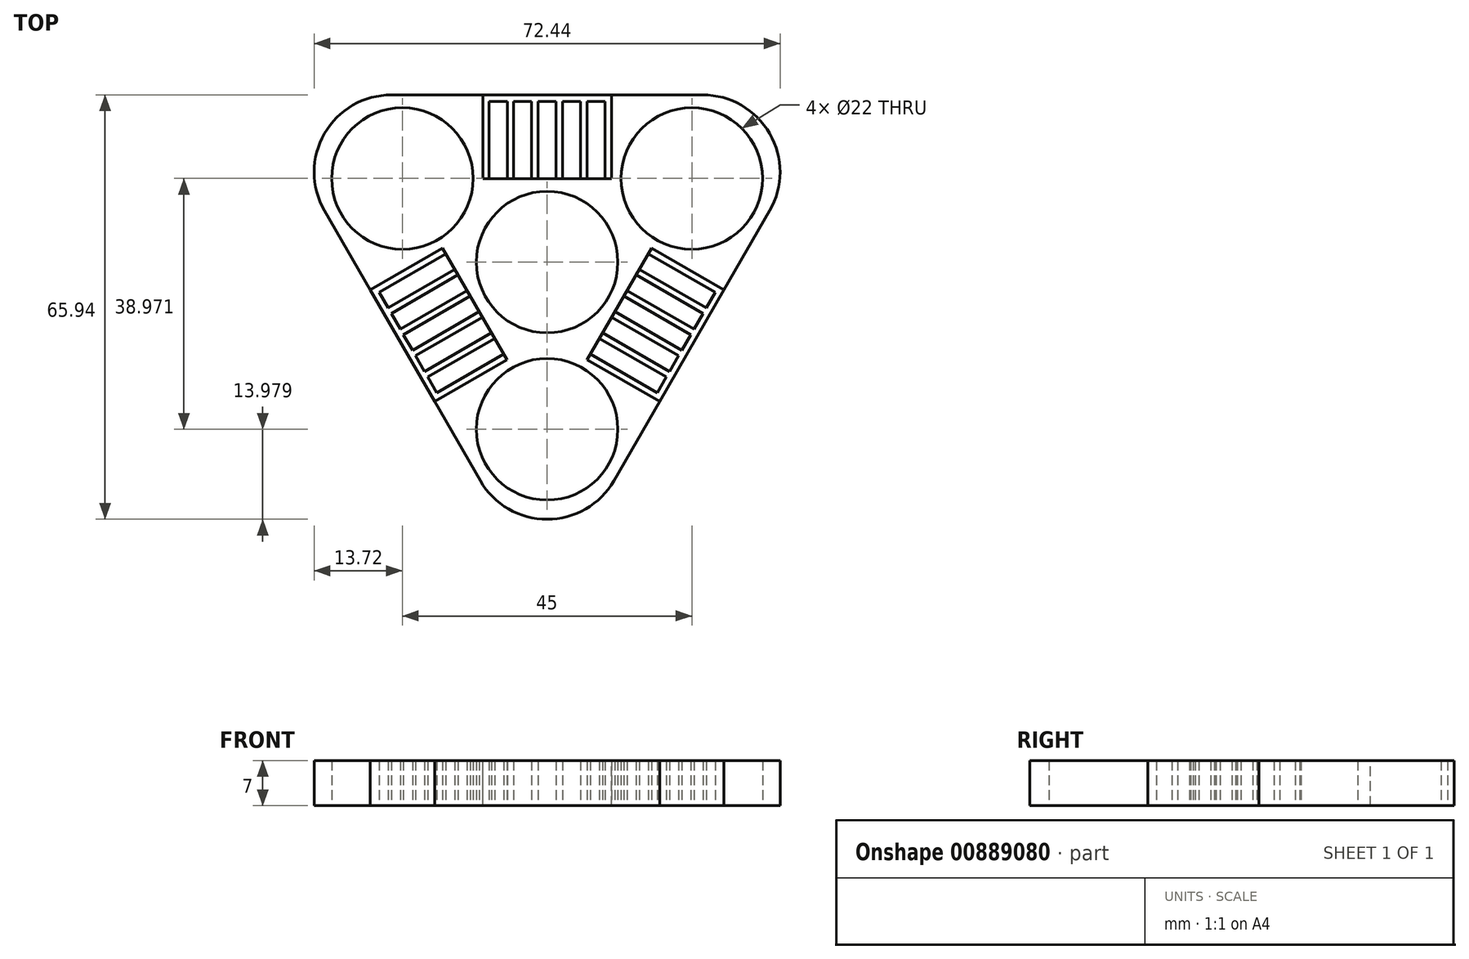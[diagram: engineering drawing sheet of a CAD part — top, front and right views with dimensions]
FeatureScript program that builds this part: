
annotation { "Feature Type Name" : "Feature", "Feature Type Description" : "" }
export const myFeature = defineFeature(function(context is Context, id is Id, definition is map)
    precondition{}
    {
        {
            var Q0;
            Q0=qCreatedBy(makeId("Top.planeOp"),FACE);
            var sketch = newSketch(context, id + "F0", { "sketchPlane" : qUnion([Q0])});
            skCircle(sketch, "E0.cCircle", {"center": v(0, 0) * mm, "radius": 25.98 * mm, "construction": true});
            skLineSegment(sketch, "E0.0", {"start": v(-45, 25.98) * mm, "end": v(45, 25.98) * mm});
            skLineSegment(sketch, "E0.1", {"start": v(45, 25.98) * mm, "end": v(0, -51.96) * mm});
            skLineSegment(sketch, "E0.2", {"start": v(0, -51.96) * mm, "end": v(-45, 25.98) * mm});
            skPoint(sketch, "E0.0.midPoint", {"position": v(0, 25.98) * mm});
            skCircle(sketch, "E1", {"center": v(0, 0) * mm, "radius": 11 * mm});
            skLineSegment(sketch, "E2", {"start": v(0, 0) * mm, "end": v(0, -51.96) * mm, "construction": true});
            skLineSegment(sketch, "E3", {"start": v(0, 0) * mm, "end": v(-45, 25.98) * mm, "construction": true});
            skLineSegment(sketch, "E4", {"start": v(0, 0) * mm, "end": v(45, 25.98) * mm, "construction": true});
            skCircle(sketch, "E5", {"center": v(-22.5, 13) * mm, "radius": 11 * mm});
            skCircle(sketch, "E6", {"center": v(0, -25.98) * mm, "radius": 11 * mm});
            skCircle(sketch, "E7", {"center": v(22.5, 13) * mm, "radius": 11 * mm});
            skSolve(sketch);
        }
        {
            var Q0;
            Q0=makeQuery(id+"F0.imprint","IMPRINT",FACE,{"disambiguationData":[TD([[makeQuery(id+"F0.imprint","IMPRINT",EDGE,{"derivedFrom":sQuery(id+"F0.wireOp",EDGE,"E0.0")}),-1.0]])]});
            extrude(context, id + "F1", {"entities" : qUnion([Q0]), "depth" : 7 * mm, "offsetDistance" : 25 * mm});
        }
        {
            var Q0;
            Q0=makeQuery(id+"F1.opExtrude","SWEPT_EDGE",EDGE,{"disambiguationData":[OSD([sQuery(id+"F0.wireOp",EDGE,"E0.0"),sQuery(id+"F0.wireOp",EDGE,"E0.2")])]});
            var Q1;
            Q1=makeQuery(id+"F1.opExtrude","SWEPT_EDGE",EDGE,{"disambiguationData":[OSD([sQuery(id+"F0.wireOp",EDGE,"E0.1"),sQuery(id+"F0.wireOp",EDGE,"E0.2")])]});
            var Q2;
            Q2=makeQuery(id+"F1.opExtrude","SWEPT_EDGE",EDGE,{"disambiguationData":[OSD([sQuery(id+"F0.wireOp",EDGE,"E0.0"),sQuery(id+"F0.wireOp",EDGE,"E0.1")])]});
            fillet(context, id + "F2", {"entities" : qUnion([Q0, Q1, Q2]), "radius" : 12 * mm, "tangentPropagation" : true, "allowEdgeOverflow" : false});
        }
        {
            var Q0;
            Q0=makeQuery(id+"F1.opExtrude","CAP_FACE",FACE,{"disambiguationData":[OSD([sQuery(id+"F0.wireOp",EDGE,"E0.0"),sQuery(id+"F0.wireOp",EDGE,"E0.1"),sQuery(id+"F0.wireOp",EDGE,"E0.2"),sQuery(id+"F0.wireOp",EDGE,"E1"),sQuery(id+"F0.wireOp",EDGE,"E5"),sQuery(id+"F0.wireOp",EDGE,"E6"),sQuery(id+"F0.wireOp",EDGE,"E7")])],"isStart":false});
            var sketch = newSketch(context, id + "F3", { "sketchPlane" : qUnion([Q0])});
            skCircle(sketch, "E8", {"center": v(0, 0) * mm, "radius": 40 * mm});
            skLineSegment(sketch, "E9.bottom", {"start": v(10, 12.98) * mm, "end": v(-10, 12.98) * mm});
            skLineSegment(sketch, "E9.top", {"start": v(10, 38.98) * mm, "end": v(-10, 38.98) * mm});
            skLineSegment(sketch, "E9.left", {"start": v(10, 12.98) * mm, "end": v(10, 38.98) * mm});
            skLineSegment(sketch, "E9.right", {"start": v(-10, 12.98) * mm, "end": v(-10, 38.98) * mm});
            skPoint(sketch, "E9.middle", {"position": v(0, 25.98) * mm});
            skLineSegment(sketch, "E10.1.0", {"start": v(-6.24, -15.15) * mm, "end": v(-28.76, -28.15) * mm});
            skLineSegment(sketch, "E10.1.1", {"start": v(-16.24, 2.17) * mm, "end": v(-6.24, -15.15) * mm});
            skLineSegment(sketch, "E10.1.2", {"start": v(-16.24, 2.17) * mm, "end": v(-38.76, -10.83) * mm});
            skLineSegment(sketch, "E10.1.3", {"start": v(-38.76, -10.83) * mm, "end": v(-28.76, -28.15) * mm});
            skLineSegment(sketch, "E10.2.0", {"start": v(16.24, 2.17) * mm, "end": v(38.76, -10.83) * mm});
            skLineSegment(sketch, "E10.2.1", {"start": v(6.24, -15.15) * mm, "end": v(16.24, 2.17) * mm});
            skLineSegment(sketch, "E10.2.2", {"start": v(6.24, -15.15) * mm, "end": v(28.76, -28.15) * mm});
            skLineSegment(sketch, "E10.2.3", {"start": v(28.76, -28.15) * mm, "end": v(38.76, -10.83) * mm});
            skSolve(sketch);
        }
        {
            var Q0;
            {var subQ0=sQuery(id+"F3.wireOp",EDGE,"E9.bottom");Q0=makeQuery(id+"F3.imprint","IMPRINT",FACE,{"disambiguationData":[TD([[makeQuery(id+"F3.imprint","IMPRINT",EDGE,{"derivedFrom":subQ0}),-1.0]])]});}
            var Q1;
            {var subQ0=sQuery(id+"F3.wireOp",EDGE,"E10.2.1");Q1=makeQuery(id+"F3.imprint","IMPRINT",FACE,{"disambiguationData":[TD([[makeQuery(id+"F3.imprint","IMPRINT",EDGE,{"derivedFrom":subQ0}),-1.0]])]});}
            var Q2;
            {var subQ0=sQuery(id+"F3.wireOp",EDGE,"E10.1.1");Q2=makeQuery(id+"F3.imprint","IMPRINT",FACE,{"disambiguationData":[TD([[makeQuery(id+"F3.imprint","IMPRINT",EDGE,{"derivedFrom":subQ0}),-1.0]])]});}
            extrude(context, id + "F4", {"entities" : qUnion([Q0, Q1, Q2]), "operationType" : NewBodyOperationType.REMOVE, "oppositeDirection" : true, "depth" : 25 * mm, "offsetDistance" : 25 * mm});
        }
        {
            var Q0;
            Q0=qCreatedBy(makeId("Top.planeOp"),FACE);
            var sketch = newSketch(context, id + "F5", { "sketchPlane" : qUnion([Q0])});
            skLineSegment(sketch, "E11.0", {"start": v(-24.22, 25.98) * mm, "end": v(-10, 25.98) * mm, "construction": true});
            skLineSegment(sketch, "E12.0", {"start": v(-10, 12.98) * mm, "end": v(-10, 25.98) * mm, "construction": true});
            skLineSegment(sketch, "E13.0", {"start": v(10, 12.98) * mm, "end": v(-10, 12.98) * mm});
            skLineSegment(sketch, "E14.0", {"start": v(10, 12.98) * mm, "end": v(10, 25.98) * mm, "construction": true});
            skLineSegment(sketch, "E15.0", {"start": v(10, 25.98) * mm, "end": v(24.22, 25.98) * mm, "construction": true});
            skLineSegment(sketch, "E16.bottom", {"start": v(-10, 25.98) * mm, "end": v(-9, 25.98) * mm});
            skLineSegment(sketch, "E16.top", {"start": v(-10, 12.98) * mm, "end": v(-9, 12.98) * mm});
            skLineSegment(sketch, "E16.left", {"start": v(-10, 25.98) * mm, "end": v(-10, 12.98) * mm});
            skLineSegment(sketch, "E16.right", {"start": v(-9, 25.98) * mm, "end": v(-9, 12.98) * mm});
            skLineSegment(sketch, "E17.1.0.0", {"start": v(-8.1, 25.98) * mm, "end": v(-8.1, 12.98) * mm});
            skLineSegment(sketch, "E17.1.0.1", {"start": v(-8.1, 25.98) * mm, "end": v(-7.1, 25.98) * mm});
            skLineSegment(sketch, "E17.1.0.2", {"start": v(-7.1, 25.98) * mm, "end": v(-7.1, 12.98) * mm});
            skLineSegment(sketch, "E17.2.0.0", {"start": v(-6.2, 25.98) * mm, "end": v(-6.2, 12.98) * mm});
            skLineSegment(sketch, "E17.2.0.1", {"start": v(-6.2, 25.98) * mm, "end": v(-5.2, 25.98) * mm});
            skLineSegment(sketch, "E17.2.0.2", {"start": v(-5.2, 25.98) * mm, "end": v(-5.2, 12.98) * mm});
            skLineSegment(sketch, "E17.3.0.0", {"start": v(-4.3, 25.98) * mm, "end": v(-4.3, 12.98) * mm});
            skLineSegment(sketch, "E17.3.0.1", {"start": v(-4.3, 25.98) * mm, "end": v(-3.3, 25.98) * mm});
            skLineSegment(sketch, "E17.3.0.2", {"start": v(-3.3, 25.98) * mm, "end": v(-3.3, 12.98) * mm});
            skLineSegment(sketch, "E17.4.0.0", {"start": v(-2.4, 25.98) * mm, "end": v(-2.4, 12.98) * mm});
            skLineSegment(sketch, "E17.4.0.1", {"start": v(-2.4, 25.98) * mm, "end": v(-1.4, 25.98) * mm});
            skLineSegment(sketch, "E17.4.0.2", {"start": v(-1.4, 25.98) * mm, "end": v(-1.4, 12.98) * mm});
            skLineSegment(sketch, "E17.5.0.0", {"start": v(-0.5, 25.98) * mm, "end": v(-0.5, 12.98) * mm});
            skLineSegment(sketch, "E17.5.0.1", {"start": v(-0.5, 25.98) * mm, "end": v(0.5, 25.98) * mm});
            skLineSegment(sketch, "E17.5.0.2", {"start": v(0.5, 25.98) * mm, "end": v(0.5, 12.98) * mm});
            skLineSegment(sketch, "E17.6.0.0", {"start": v(1.4, 25.98) * mm, "end": v(1.4, 12.98) * mm});
            skLineSegment(sketch, "E17.6.0.1", {"start": v(1.4, 25.98) * mm, "end": v(2.4, 25.98) * mm});
            skLineSegment(sketch, "E17.6.0.2", {"start": v(2.4, 25.98) * mm, "end": v(2.4, 12.98) * mm});
            skLineSegment(sketch, "E17.7.0.0", {"start": v(3.3, 25.98) * mm, "end": v(3.3, 12.98) * mm});
            skLineSegment(sketch, "E17.7.0.1", {"start": v(3.3, 25.98) * mm, "end": v(4.3, 25.98) * mm});
            skLineSegment(sketch, "E17.7.0.2", {"start": v(4.3, 25.98) * mm, "end": v(4.3, 12.98) * mm});
            skLineSegment(sketch, "E17.8.0.0", {"start": v(5.2, 25.98) * mm, "end": v(5.2, 12.98) * mm});
            skLineSegment(sketch, "E17.8.0.1", {"start": v(5.2, 25.98) * mm, "end": v(6.2, 25.98) * mm});
            skLineSegment(sketch, "E17.8.0.2", {"start": v(6.2, 25.98) * mm, "end": v(6.2, 12.98) * mm});
            skLineSegment(sketch, "E17.9.0.0", {"start": v(7.1, 25.98) * mm, "end": v(7.1, 12.98) * mm});
            skLineSegment(sketch, "E17.9.0.1", {"start": v(7.1, 25.98) * mm, "end": v(8.1, 25.98) * mm});
            skLineSegment(sketch, "E17.9.0.2", {"start": v(8.1, 25.98) * mm, "end": v(8.1, 12.98) * mm});
            skLineSegment(sketch, "E17.direction1", {"start": v(-10, 12.98) * mm, "end": v(-8.1, 12.98) * mm, "construction": true});
            skLineSegment(sketch, "E18.bottom", {"start": v(-10, 25.98) * mm, "end": v(10, 25.98) * mm});
            skLineSegment(sketch, "E18.top", {"start": v(-10, 24.98) * mm, "end": v(10, 24.98) * mm});
            skLineSegment(sketch, "E18.left", {"start": v(-10, 25.98) * mm, "end": v(-10, 24.98) * mm});
            skLineSegment(sketch, "E18.right", {"start": v(10, 25.98) * mm, "end": v(10, 24.98) * mm});
            skLineSegment(sketch, "E19.0.10.0", {"start": v(9, 25.98) * mm, "end": v(9, 12.98) * mm});
            skLineSegment(sketch, "E19.3.10.0", {"start": v(9, 25.98) * mm, "end": v(10, 25.98) * mm});
            skLineSegment(sketch, "E19.6.10.0", {"start": v(10, 25.98) * mm, "end": v(10, 12.98) * mm});
            skSolve(sketch);
        }
        {
            var Q0;
            {var subQ0=sQuery(id+"F5.wireOp",EDGE,"E16.left");var subQ1=sQuery(id+"F5.wireOp",EDGE,"E13.0");var subQ2=makeQuery(id+"F5.imprint","INTERSECT",VERTEX,{"derivedFrom":[subQ1,subQ0]});Q0=makeQuery(id+"F5.imprint","IMPRINT",FACE,{"disambiguationData":[TD([[makeQuery(id+"F5.imprint","IMPRINT",EDGE,{"disambiguationData":[TD([[subQ2,1.0]])],"derivedFrom":subQ1}),-1.0]])]});}
            var Q1;
            {var subQ0=sQuery(id+"F5.wireOp",EDGE,"E17.2.0.2");var subQ1=sQuery(id+"F5.wireOp",EDGE,"E13.0");var subQ2=makeQuery(id+"F5.imprint","INTERSECT",VERTEX,{"derivedFrom":[subQ1,subQ0]});Q1=makeQuery(id+"F5.imprint","IMPRINT",FACE,{"disambiguationData":[TD([[makeQuery(id+"F5.imprint","IMPRINT",EDGE,{"disambiguationData":[TD([[subQ2,-1.0]])],"derivedFrom":subQ1}),-1.0]])]});}
            var Q2;
            {var subQ0=sQuery(id+"F5.wireOp",EDGE,"E17.4.0.0");var subQ1=sQuery(id+"F5.wireOp",EDGE,"E13.0");var subQ2=makeQuery(id+"F5.imprint","INTERSECT",VERTEX,{"derivedFrom":[subQ1,subQ0]});Q2=makeQuery(id+"F5.imprint","IMPRINT",FACE,{"disambiguationData":[TD([[makeQuery(id+"F5.imprint","IMPRINT",EDGE,{"disambiguationData":[TD([[subQ2,1.0]])],"derivedFrom":subQ1}),-1.0]])]});}
            var Q3;
            {var subQ0=sQuery(id+"F5.wireOp",EDGE,"E17.6.0.0");var subQ1=sQuery(id+"F5.wireOp",EDGE,"E13.0");var subQ2=makeQuery(id+"F5.imprint","INTERSECT",VERTEX,{"derivedFrom":[subQ1,subQ0]});Q3=makeQuery(id+"F5.imprint","IMPRINT",FACE,{"disambiguationData":[TD([[makeQuery(id+"F5.imprint","IMPRINT",EDGE,{"disambiguationData":[TD([[subQ2,1.0]])],"derivedFrom":subQ1}),-1.0]])]});}
            var Q4;
            {var subQ0=sQuery(id+"F5.wireOp",EDGE,"E17.8.0.2");var subQ1=sQuery(id+"F5.wireOp",EDGE,"E13.0");var subQ2=makeQuery(id+"F5.imprint","INTERSECT",VERTEX,{"derivedFrom":[subQ1,subQ0]});Q4=makeQuery(id+"F5.imprint","IMPRINT",FACE,{"disambiguationData":[TD([[makeQuery(id+"F5.imprint","IMPRINT",EDGE,{"disambiguationData":[TD([[subQ2,-1.0]])],"derivedFrom":subQ1}),-1.0]])]});}
            var Q5;
            {var subQ0=sQuery(id+"F5.wireOp",EDGE,"E19.6.10.0");Q5=makeQuery(id+"F5.imprint","IMPRINT",FACE,{"disambiguationData":[TD([[makeQuery(id+"F5.imprint","IMPRINT",EDGE,{"derivedFrom":subQ0}),-1.0]])]});}
            var Q6;
            {var subQ3=sQuery(id+"F5.wireOp",EDGE,"E18.right");Q6=makeQuery(id+"F5.imprint","IMPRINT",FACE,{"disambiguationData":[TD([[makeQuery(id+"F5.imprint","IMPRINT",EDGE,{"derivedFrom":subQ3}),-1.0]])]});}
            var Q7;
            {var subQ1=sQuery(id+"F5.wireOp",EDGE,"E17.9.0.2");var subQ3=sQuery(id+"F5.wireOp",EDGE,"E18.top");var subQ4=makeQuery(id+"F5.imprint","INTERSECT",VERTEX,{"derivedFrom":[subQ1,subQ3]});Q7=makeQuery(id+"F5.imprint","IMPRINT",FACE,{"disambiguationData":[TD([[makeQuery(id+"F5.imprint","IMPRINT",EDGE,{"disambiguationData":[TD([[subQ4,-1.0]])],"derivedFrom":subQ3}),1.0]])]});}
            var Q8;
            {var subQ4=sQuery(id+"F5.wireOp",EDGE,"E17.9.0.1");Q8=makeQuery(id+"F5.imprint","IMPRINT",FACE,{"disambiguationData":[TD([[makeQuery(id+"F5.imprint","IMPRINT",EDGE,{"derivedFrom":subQ4}),-1.0]])]});}
            var Q9;
            {var subQ1=sQuery(id+"F5.wireOp",EDGE,"E17.8.0.2");var subQ3=sQuery(id+"F5.wireOp",EDGE,"E18.top");var subQ4=makeQuery(id+"F5.imprint","INTERSECT",VERTEX,{"derivedFrom":[subQ1,subQ3]});Q9=makeQuery(id+"F5.imprint","IMPRINT",FACE,{"disambiguationData":[TD([[makeQuery(id+"F5.imprint","IMPRINT",EDGE,{"disambiguationData":[TD([[subQ4,-1.0]])],"derivedFrom":subQ3}),1.0]])]});}
            var Q10;
            {var subQ4=sQuery(id+"F5.wireOp",EDGE,"E17.8.0.1");Q10=makeQuery(id+"F5.imprint","IMPRINT",FACE,{"disambiguationData":[TD([[makeQuery(id+"F5.imprint","IMPRINT",EDGE,{"derivedFrom":subQ4}),-1.0]])]});}
            var Q11;
            {var subQ1=sQuery(id+"F5.wireOp",EDGE,"E17.7.0.2");var subQ3=sQuery(id+"F5.wireOp",EDGE,"E18.top");var subQ4=makeQuery(id+"F5.imprint","INTERSECT",VERTEX,{"derivedFrom":[subQ1,subQ3]});Q11=makeQuery(id+"F5.imprint","IMPRINT",FACE,{"disambiguationData":[TD([[makeQuery(id+"F5.imprint","IMPRINT",EDGE,{"disambiguationData":[TD([[subQ4,-1.0]])],"derivedFrom":subQ3}),1.0]])]});}
            var Q12;
            {var subQ4=sQuery(id+"F5.wireOp",EDGE,"E17.7.0.1");Q12=makeQuery(id+"F5.imprint","IMPRINT",FACE,{"disambiguationData":[TD([[makeQuery(id+"F5.imprint","IMPRINT",EDGE,{"derivedFrom":subQ4}),-1.0]])]});}
            var Q13;
            {var subQ1=sQuery(id+"F5.wireOp",EDGE,"E17.6.0.2");var subQ3=sQuery(id+"F5.wireOp",EDGE,"E18.top");var subQ4=makeQuery(id+"F5.imprint","INTERSECT",VERTEX,{"derivedFrom":[subQ1,subQ3]});Q13=makeQuery(id+"F5.imprint","IMPRINT",FACE,{"disambiguationData":[TD([[makeQuery(id+"F5.imprint","IMPRINT",EDGE,{"disambiguationData":[TD([[subQ4,-1.0]])],"derivedFrom":subQ3}),1.0]])]});}
            var Q14;
            {var subQ4=sQuery(id+"F5.wireOp",EDGE,"E17.6.0.1");Q14=makeQuery(id+"F5.imprint","IMPRINT",FACE,{"disambiguationData":[TD([[makeQuery(id+"F5.imprint","IMPRINT",EDGE,{"derivedFrom":subQ4}),-1.0]])]});}
            var Q15;
            {var subQ1=sQuery(id+"F5.wireOp",EDGE,"E17.5.0.2");var subQ3=sQuery(id+"F5.wireOp",EDGE,"E18.top");var subQ4=makeQuery(id+"F5.imprint","INTERSECT",VERTEX,{"derivedFrom":[subQ1,subQ3]});Q15=makeQuery(id+"F5.imprint","IMPRINT",FACE,{"disambiguationData":[TD([[makeQuery(id+"F5.imprint","IMPRINT",EDGE,{"disambiguationData":[TD([[subQ4,-1.0]])],"derivedFrom":subQ3}),1.0]])]});}
            var Q16;
            {var subQ4=sQuery(id+"F5.wireOp",EDGE,"E17.5.0.1");Q16=makeQuery(id+"F5.imprint","IMPRINT",FACE,{"disambiguationData":[TD([[makeQuery(id+"F5.imprint","IMPRINT",EDGE,{"derivedFrom":subQ4}),-1.0]])]});}
            var Q17;
            {var subQ1=sQuery(id+"F5.wireOp",EDGE,"E17.4.0.2");var subQ3=sQuery(id+"F5.wireOp",EDGE,"E18.top");var subQ4=makeQuery(id+"F5.imprint","INTERSECT",VERTEX,{"derivedFrom":[subQ1,subQ3]});Q17=makeQuery(id+"F5.imprint","IMPRINT",FACE,{"disambiguationData":[TD([[makeQuery(id+"F5.imprint","IMPRINT",EDGE,{"disambiguationData":[TD([[subQ4,-1.0]])],"derivedFrom":subQ3}),1.0]])]});}
            var Q18;
            {var subQ4=sQuery(id+"F5.wireOp",EDGE,"E17.4.0.1");Q18=makeQuery(id+"F5.imprint","IMPRINT",FACE,{"disambiguationData":[TD([[makeQuery(id+"F5.imprint","IMPRINT",EDGE,{"derivedFrom":subQ4}),-1.0]])]});}
            var Q19;
            {var subQ1=sQuery(id+"F5.wireOp",EDGE,"E17.3.0.2");var subQ3=sQuery(id+"F5.wireOp",EDGE,"E18.top");var subQ4=makeQuery(id+"F5.imprint","INTERSECT",VERTEX,{"derivedFrom":[subQ1,subQ3]});Q19=makeQuery(id+"F5.imprint","IMPRINT",FACE,{"disambiguationData":[TD([[makeQuery(id+"F5.imprint","IMPRINT",EDGE,{"disambiguationData":[TD([[subQ4,-1.0]])],"derivedFrom":subQ3}),1.0]])]});}
            var Q20;
            {var subQ4=sQuery(id+"F5.wireOp",EDGE,"E17.3.0.1");Q20=makeQuery(id+"F5.imprint","IMPRINT",FACE,{"disambiguationData":[TD([[makeQuery(id+"F5.imprint","IMPRINT",EDGE,{"derivedFrom":subQ4}),-1.0]])]});}
            var Q21;
            {var subQ1=sQuery(id+"F5.wireOp",EDGE,"E17.2.0.2");var subQ3=sQuery(id+"F5.wireOp",EDGE,"E18.top");var subQ4=makeQuery(id+"F5.imprint","INTERSECT",VERTEX,{"derivedFrom":[subQ1,subQ3]});Q21=makeQuery(id+"F5.imprint","IMPRINT",FACE,{"disambiguationData":[TD([[makeQuery(id+"F5.imprint","IMPRINT",EDGE,{"disambiguationData":[TD([[subQ4,-1.0]])],"derivedFrom":subQ3}),1.0]])]});}
            var Q22;
            {var subQ4=sQuery(id+"F5.wireOp",EDGE,"E17.2.0.1");Q22=makeQuery(id+"F5.imprint","IMPRINT",FACE,{"disambiguationData":[TD([[makeQuery(id+"F5.imprint","IMPRINT",EDGE,{"derivedFrom":subQ4}),-1.0]])]});}
            var Q23;
            {var subQ1=sQuery(id+"F5.wireOp",EDGE,"E17.1.0.2");var subQ3=sQuery(id+"F5.wireOp",EDGE,"E18.top");var subQ4=makeQuery(id+"F5.imprint","INTERSECT",VERTEX,{"derivedFrom":[subQ1,subQ3]});Q23=makeQuery(id+"F5.imprint","IMPRINT",FACE,{"disambiguationData":[TD([[makeQuery(id+"F5.imprint","IMPRINT",EDGE,{"disambiguationData":[TD([[subQ4,-1.0]])],"derivedFrom":subQ3}),1.0]])]});}
            var Q24;
            {var subQ4=sQuery(id+"F5.wireOp",EDGE,"E17.1.0.1");Q24=makeQuery(id+"F5.imprint","IMPRINT",FACE,{"disambiguationData":[TD([[makeQuery(id+"F5.imprint","IMPRINT",EDGE,{"derivedFrom":subQ4}),-1.0]])]});}
            var Q25;
            {var subQ1=sQuery(id+"F5.wireOp",EDGE,"E16.right");var subQ3=sQuery(id+"F5.wireOp",EDGE,"E18.top");var subQ4=makeQuery(id+"F5.imprint","INTERSECT",VERTEX,{"derivedFrom":[subQ1,subQ3]});Q25=makeQuery(id+"F5.imprint","IMPRINT",FACE,{"disambiguationData":[TD([[makeQuery(id+"F5.imprint","IMPRINT",EDGE,{"disambiguationData":[TD([[subQ4,-1.0]])],"derivedFrom":subQ3}),1.0]])]});}
            var Q26;
            {var subQ0=sQuery(id+"F5.wireOp",EDGE,"E16.bottom");Q26=makeQuery(id+"F5.imprint","IMPRINT",FACE,{"disambiguationData":[TD([[makeQuery(id+"F5.imprint","IMPRINT",EDGE,{"derivedFrom":subQ0}),-1.0]])]});}
            extrude(context, id + "F6", {"entities" : qUnion([Q0, Q1, Q2, Q3, Q4, Q5, Q6, Q7, Q8, Q9, Q10, Q11, Q12, Q13, Q14, Q15, Q16, Q17, Q18, Q19, Q20, Q21, Q22, Q23, Q24, Q25, Q26]), "depth" : 7 * mm, "offsetDistance" : 25 * mm});
        }
        {
            var Q0;
            Q0=qCreatedBy(makeId("Front.planeOp"),FACE);
            var sketch = newSketch(context, id + "F7", { "sketchPlane" : qUnion([Q0])});
            skLineSegment(sketch, "E20", {"start": v(0, 0) * mm, "end": v(0, 14.57) * mm});
            skSolve(sketch);
        }
        {
            var Q0;
            Q0=makeQuery(id+"F6.opExtrude","SWEPT_BODY",BODY,{"disambiguationData":[OSD([sQuery(id+"F5.wireOp",EDGE,"E13.0"),sQuery(id+"F5.wireOp",EDGE,"E16.bottom"),sQuery(id+"F5.wireOp",EDGE,"E16.left"),sQuery(id+"F5.wireOp",EDGE,"E16.right"),sQuery(id+"F5.wireOp",EDGE,"E17.1.0.1"),sQuery(id+"F5.wireOp",EDGE,"E17.2.0.0"),sQuery(id+"F5.wireOp",EDGE,"E17.2.0.1"),sQuery(id+"F5.wireOp",EDGE,"E17.2.0.2"),sQuery(id+"F5.wireOp",EDGE,"E17.3.0.1"),sQuery(id+"F5.wireOp",EDGE,"E17.4.0.0"),sQuery(id+"F5.wireOp",EDGE,"E17.4.0.1"),sQuery(id+"F5.wireOp",EDGE,"E17.4.0.2"),sQuery(id+"F5.wireOp",EDGE,"E17.5.0.1"),sQuery(id+"F5.wireOp",EDGE,"E17.6.0.0"),sQuery(id+"F5.wireOp",EDGE,"E17.6.0.1"),sQuery(id+"F5.wireOp",EDGE,"E17.6.0.2"),sQuery(id+"F5.wireOp",EDGE,"E17.7.0.1"),sQuery(id+"F5.wireOp",EDGE,"E17.8.0.0"),sQuery(id+"F5.wireOp",EDGE,"E17.8.0.1"),sQuery(id+"F5.wireOp",EDGE,"E17.8.0.2"),sQuery(id+"F5.wireOp",EDGE,"E17.9.0.1"),sQuery(id+"F5.wireOp",EDGE,"E18.bottom"),sQuery(id+"F5.wireOp",EDGE,"E18.top"),sQuery(id+"F5.wireOp",EDGE,"E18.right"),sQuery(id+"F5.wireOp",EDGE,"E19.0.10.0"),sQuery(id+"F5.wireOp",EDGE,"E19.6.10.0")])]});
            var Q1;
            Q1=sQuery(id+"F7.wireOp",EDGE,"E20");
            circularPattern(context, id + "F8", {"entities" : qUnion([Q0]), "axis" : qUnion([Q1]), "angle" : 360 * degree, "instanceCount" : 3, "equalSpace" : true});
        }
    });
